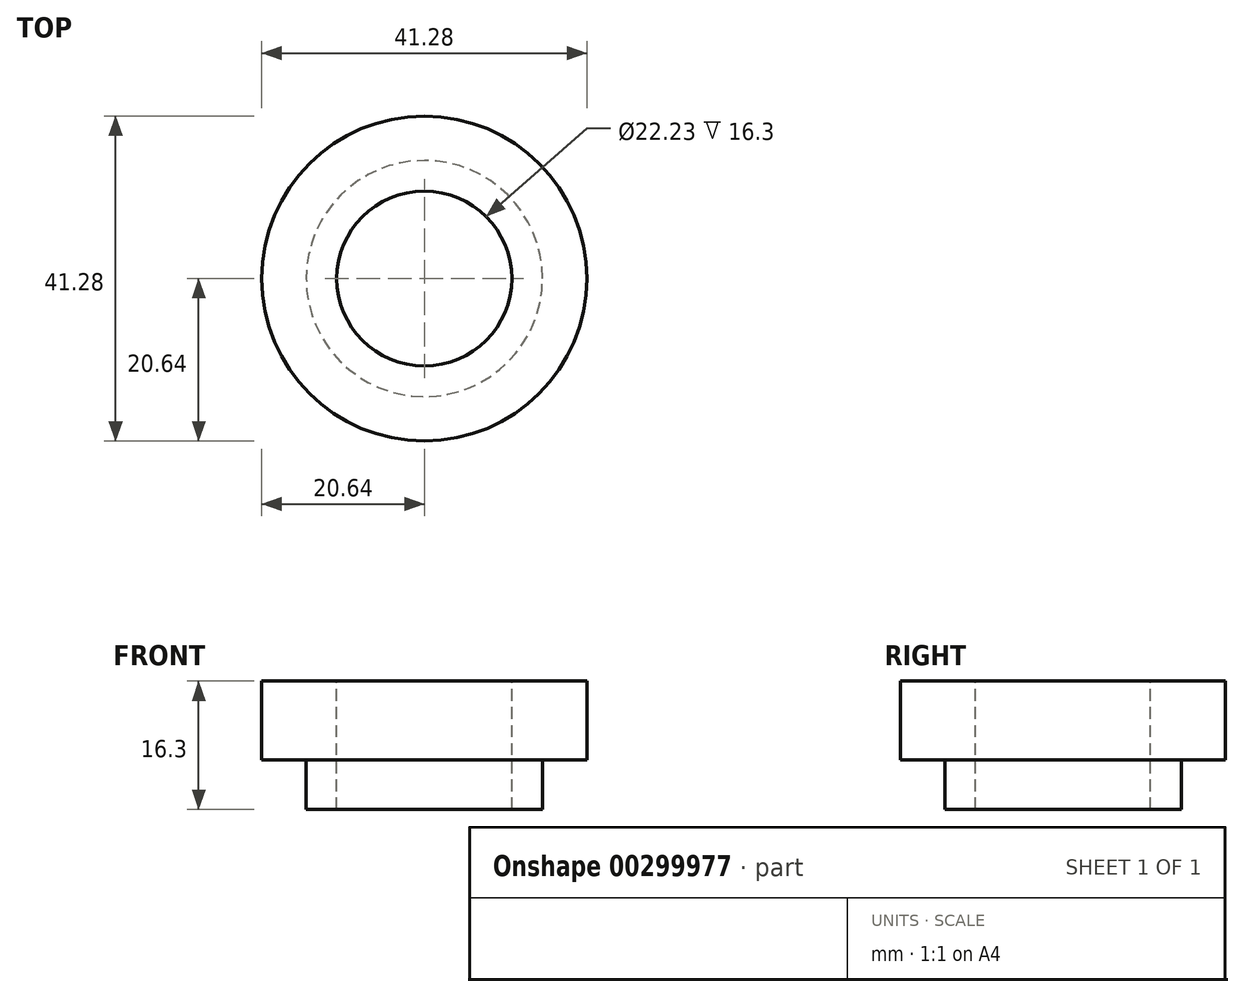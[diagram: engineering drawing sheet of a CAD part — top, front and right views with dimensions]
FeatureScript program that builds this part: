
annotation { "Feature Type Name" : "Feature", "Feature Type Description" : "" }
export const myFeature = defineFeature(function(context is Context, id is Id, definition is map)
    precondition{}
    {
        {
            var Q0;
            Q0=qCreatedBy(makeId("Top.planeOp"),FACE);
            var sketch = newSketch(context, id + "F0", { "sketchPlane" : qUnion([Q0])});
            skCircle(sketch, "E0", {"center": v(0, 0) * mm, "radius": 20.64 * mm});
            skSolve(sketch);
        }
        {
            var Q0;
            Q0 = qSketchRegion(id + "F0", true);
            extrude(context, id + "F1", {"entities" : qUnion([Q0]), "depth" : 10 * mm, "offsetDistance" : 25 * mm});
        }
        {
            var Q0;
            Q0=qCreatedBy(makeId("Top.planeOp"),FACE);
            var sketch = newSketch(context, id + "F2", { "sketchPlane" : qUnion([Q0])});
            skCircle(sketch, "E1", {"center": v(0, 0) * mm, "radius": 15 * mm});
            skSolve(sketch);
        }
        {
            var Q0;
            Q0 = qSketchRegion(id + "F2", true);
            extrude(context, id + "F3", {"entities" : qUnion([Q0]), "operationType" : NewBodyOperationType.ADD, "endBound" : BoundingType.SYMMETRIC, "depth" : 12.6 * mm, "offsetDistance" : 25 * mm});
        }
        {
            var Q0;
            Q0=qCreatedBy(makeId("Top.planeOp"),FACE);
            var sketch = newSketch(context, id + "F4", { "sketchPlane" : qUnion([Q0])});
            skCircle(sketch, "E2", {"center": v(0, 0) * mm, "radius": 11.12 * mm});
            skSolve(sketch);
        }
        {
            var Q0;
            Q0 = qSketchRegion(id + "F4", true);
            extrude(context, id + "F5", {"entities" : qUnion([Q0]), "operationType" : NewBodyOperationType.REMOVE, "endBound" : BoundingType.SYMMETRIC, "oppositeDirection" : true, "depth" : 25 * mm, "offsetDistance" : 25 * mm});
        }
    });
